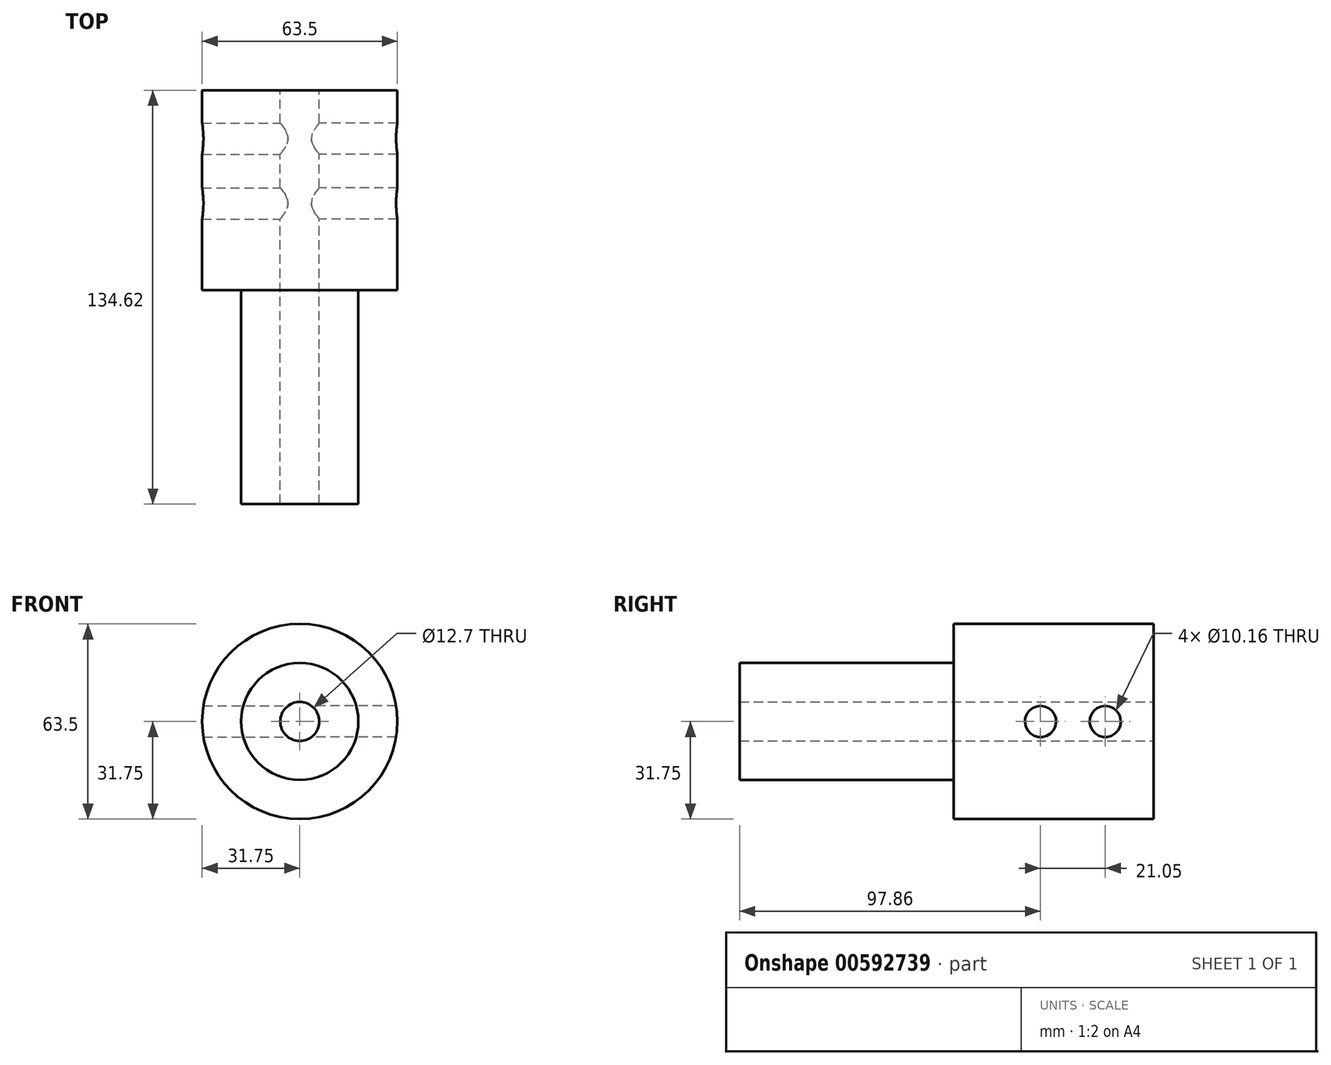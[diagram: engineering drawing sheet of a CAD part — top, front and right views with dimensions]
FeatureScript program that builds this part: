
annotation { "Feature Type Name" : "Feature", "Feature Type Description" : "" }
export const myFeature = defineFeature(function(context is Context, id is Id, definition is map)
    precondition{}
    {
        {
            var Q0;
            Q0=qCreatedBy(makeId("Front.planeOp"),FACE);
            var sketch = newSketch(context, id + "F0", { "sketchPlane" : qUnion([Q0])});
            skCircle(sketch, "E0", {"center": v(0, 0) * mm, "radius": 31.75 * mm});
            skCircle(sketch, "E1", {"center": v(0, 0) * mm, "radius": 19.05 * mm});
            skCircle(sketch, "E2", {"center": v(0, 0) * mm, "radius": 6.35 * mm});
            skSolve(sketch);
        }
        {
            var Q0;
            Q0=makeQuery(id+"F0.imprint","IMPRINT",FACE,{"disambiguationData":[TD([[makeQuery(id+"F0.imprint","IMPRINT",EDGE,{"derivedFrom":sQuery(id+"F0.wireOp",EDGE,"E1")}),1.0]])]});
            extrude(context, id + "F1", {"entities" : qUnion([Q0]), "depth" : 134.62 * mm, "offsetDistance" : 25.4 * mm});
        }
        {
            var Q0;
            Q0 = qSketchRegion(id + "F0", true);
            extrude(context, id + "F2", {"entities" : qUnion([Q0]), "operationType" : NewBodyOperationType.ADD, "depth" : 65.02 * mm, "offsetDistance" : 25.4 * mm});
        }
        {
            var Q0;
            Q0=qCreatedBy(makeId("Right.planeOp"),FACE);
            var sketch = newSketch(context, id + "F3", { "sketchPlane" : qUnion([Q0])});
            skPoint(sketch, "E3", {"position": v(-15.7, 0) * mm});
            skCircle(sketch, "E4", {"center": v(-15.7, 0) * mm, "radius": 5.08 * mm});
            skLineSegment(sketch, "E5", {"start": v(-26.23, -39.5) * mm, "end": v(-26.23, 41.5) * mm, "construction": true});
            skCircle(sketch, "E6.MirrorC", {"center": v(-36.76, 0) * mm, "radius": 5.08 * mm});
            skPoint(sketch, "E7.end.orphan", {"position": v(-52.68, -39.5) * mm});
            skPoint(sketch, "E7.start.orphan", {"position": v(-52.68, 41.5) * mm});
            skSolve(sketch);
        }
        {
            var Q0;
            Q0 = qSketchRegion(id + "F3", true);
            extrude(context, id + "F4", {"entities" : qUnion([Q0]), "operationType" : NewBodyOperationType.REMOVE, "oppositeDirection" : true, "depth" : 114.3 * mm, "offsetDistance" : 25.4 * mm});
        }
        {
            var Q0;
            Q0 = qSketchRegion(id + "F3", true);
            extrude(context, id + "F5", {"entities" : qUnion([Q0]), "operationType" : NewBodyOperationType.REMOVE, "depth" : 89.66 * mm, "offsetDistance" : 25.4 * mm});
        }
    });
